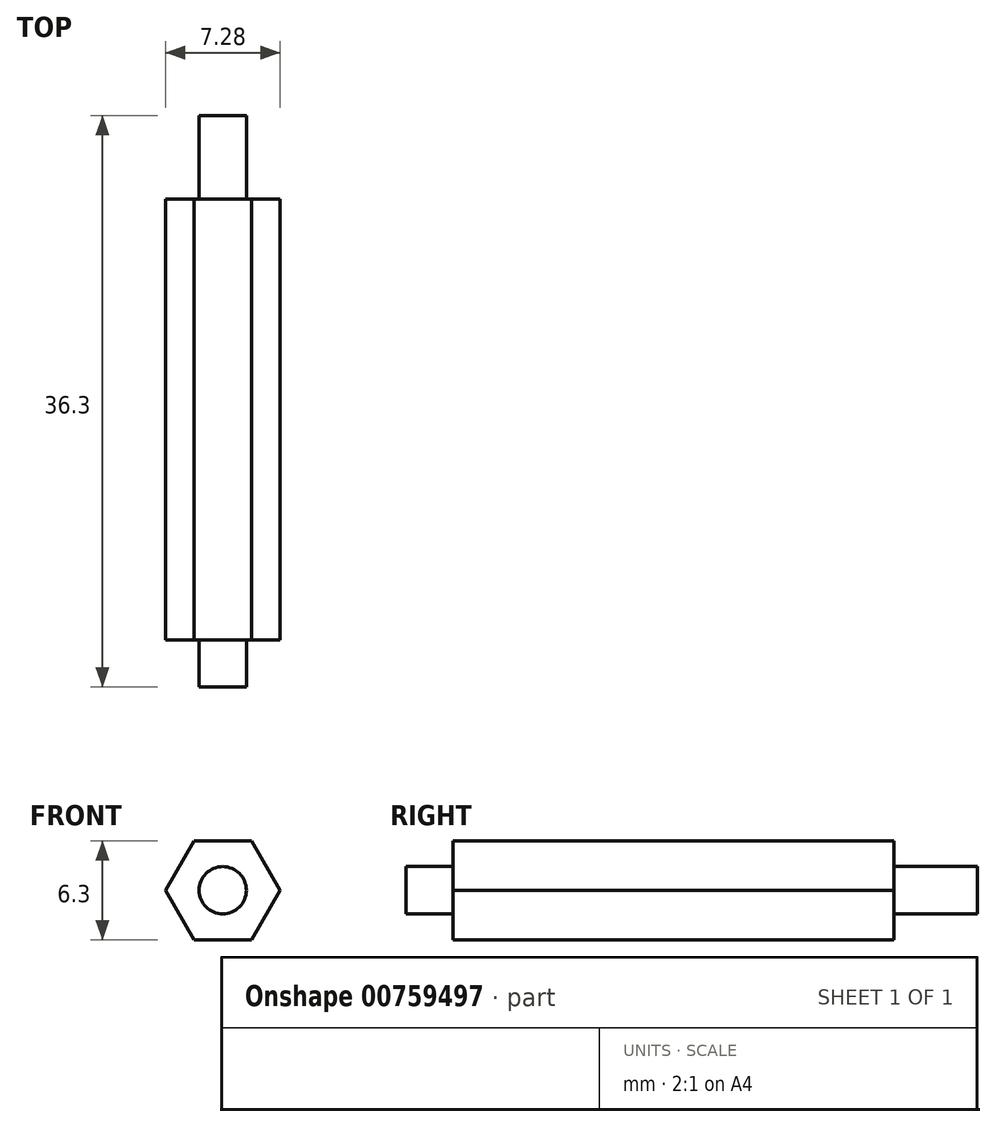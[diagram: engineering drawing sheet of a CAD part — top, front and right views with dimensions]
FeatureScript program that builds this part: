
annotation { "Feature Type Name" : "Feature", "Feature Type Description" : "" }
export const myFeature = defineFeature(function(context is Context, id is Id, definition is map)
    precondition{}
    {
        {
            var Q0;
            Q0=qCreatedBy(makeId("Front.planeOp"),FACE);
            var sketch = newSketch(context, id + "F0", { "sketchPlane" : qUnion([Q0])});
            skCircle(sketch, "E0.cCircle", {"center": v(0, 0) * mm, "radius": 3.15 * mm, "construction": true});
            skLineSegment(sketch, "E0.0", {"start": v(-1.82, 3.15) * mm, "end": v(1.82, 3.15) * mm});
            skLineSegment(sketch, "E0.1", {"start": v(1.82, 3.15) * mm, "end": v(3.64, 0) * mm});
            skLineSegment(sketch, "E0.2", {"start": v(3.64, 0) * mm, "end": v(1.82, -3.15) * mm});
            skLineSegment(sketch, "E0.3", {"start": v(1.82, -3.15) * mm, "end": v(-1.82, -3.15) * mm});
            skLineSegment(sketch, "E0.4", {"start": v(-1.82, -3.15) * mm, "end": v(-3.64, 0) * mm});
            skLineSegment(sketch, "E0.5", {"start": v(-3.64, 0) * mm, "end": v(-1.82, 3.15) * mm});
            skPoint(sketch, "E0.0.midPoint", {"position": v(0, 3.15) * mm});
            skSolve(sketch);
        }
        {
            var Q0;
            Q0 = qSketchRegion(id + "F0", true);
            extrude(context, id + "F1", {"entities" : qUnion([Q0]), "depth" : 28 * mm, "offsetDistance" : 25 * mm});
        }
        {
            var Q0;
            Q0=qCreatedBy(makeId("Front.planeOp"),FACE);
            var sketch = newSketch(context, id + "F2", { "sketchPlane" : qUnion([Q0])});
            skCircle(sketch, "E1", {"center": v(0, 0) * mm, "radius": 1.5 * mm});
            skSolve(sketch);
        }
        {
            var Q0;
            Q0 = qSketchRegion(id + "F2", true);
            extrude(context, id + "F3", {"entities" : qUnion([Q0]), "operationType" : NewBodyOperationType.ADD, "oppositeDirection" : true, "depth" : 5.3 * mm, "offsetDistance" : 25 * mm});
        }
        {
            var Q0;
            Q0=qCreatedBy(makeId("Front.planeOp"),FACE);
            var sketch = newSketch(context, id + "F4", { "sketchPlane" : qUnion([Q0])});
            skCircle(sketch, "E2", {"center": v(0, 0) * mm, "radius": 1.5 * mm});
            skSolve(sketch);
        }
        {
            var Q0;
            Q0 = qSketchRegion(id + "F4", true);
            extrude(context, id + "F5", {"entities" : qUnion([Q0]), "operationType" : NewBodyOperationType.ADD, "depth" : 31 * mm, "offsetDistance" : 25 * mm});
        }
    });
